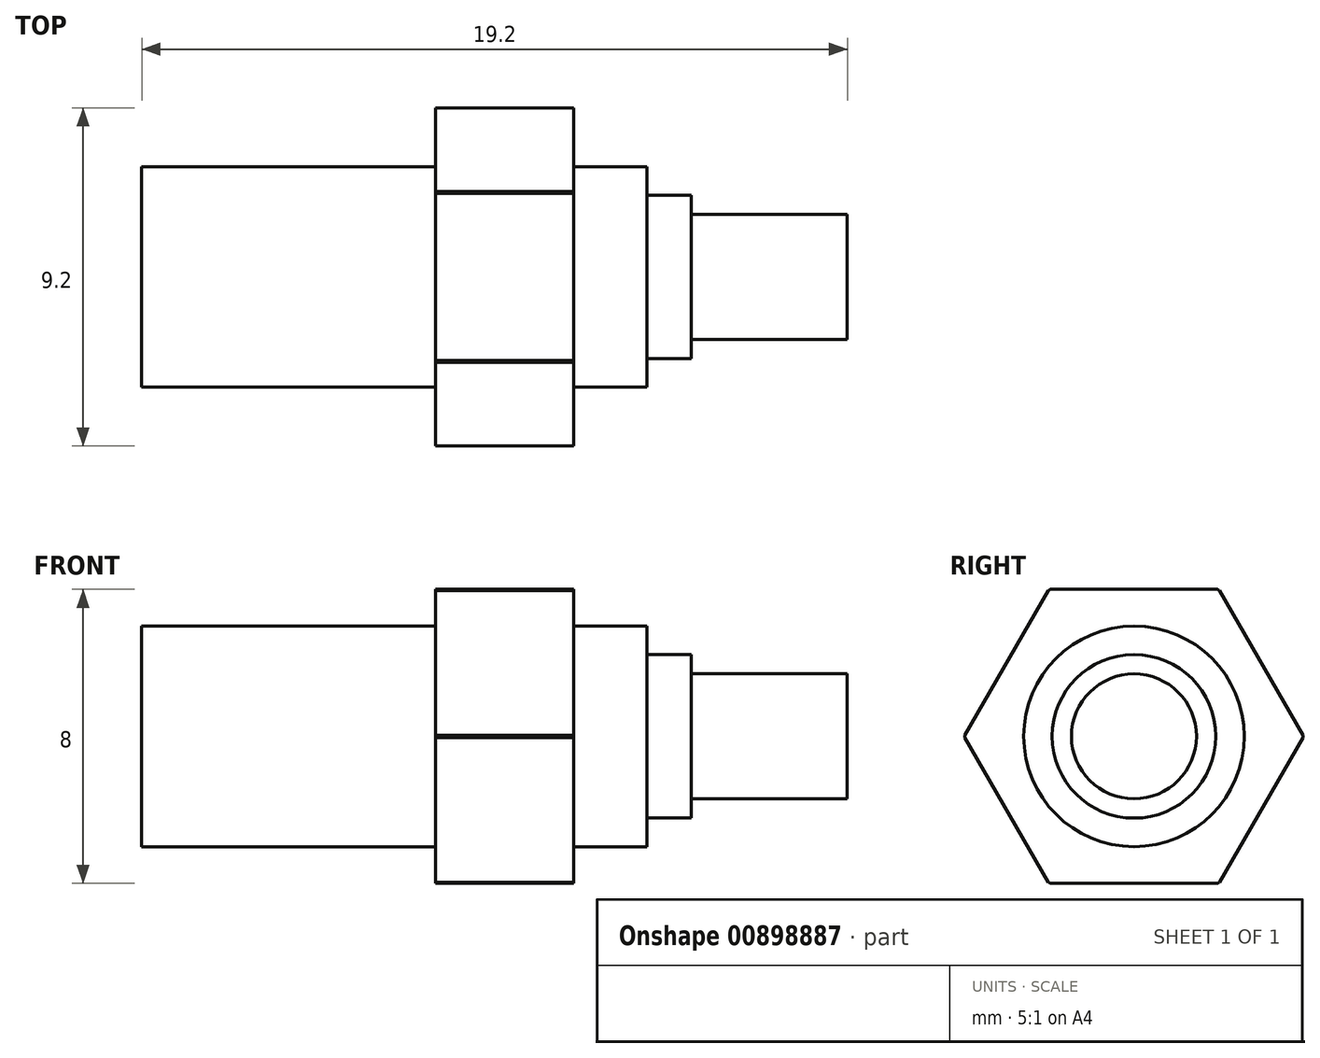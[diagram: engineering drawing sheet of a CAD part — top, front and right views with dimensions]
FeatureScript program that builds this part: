
annotation { "Feature Type Name" : "Feature", "Feature Type Description" : "" }
export const myFeature = defineFeature(function(context is Context, id is Id, definition is map)
    precondition{}
    {
        {
            var Q0;
            Q0=qCreatedBy(makeId("Top.planeOp"),FACE);
            var sketch = newSketch(context, id + "F0", { "sketchPlane" : qUnion([Q0])});
            skLineSegment(sketch, "E0", {"start": v(-9.92, 0) * mm, "end": v(9.28, 0) * mm});
            skLineSegment(sketch, "E1", {"start": v(9.28, 0) * mm, "end": v(9.28, 1.7) * mm});
            skLineSegment(sketch, "E2", {"start": v(9.28, 1.7) * mm, "end": v(5.03, 1.7) * mm});
            skLineSegment(sketch, "E3", {"start": v(5.03, 1.7) * mm, "end": v(5.03, 2.23) * mm});
            skLineSegment(sketch, "E4", {"start": v(5.03, 2.22) * mm, "end": v(3.83, 2.22) * mm});
            skLineSegment(sketch, "E5", {"start": v(3.83, 2.22) * mm, "end": v(3.83, 3) * mm});
            skLineSegment(sketch, "E6", {"start": v(3.83, 3) * mm, "end": v(1.83, 3) * mm});
            skLineSegment(sketch, "E7", {"start": v(1.83, 3) * mm, "end": v(1.83, 4.6) * mm});
            skLineSegment(sketch, "E8", {"start": v(1.83, 4.6) * mm, "end": v(-1.92, 4.6) * mm});
            skLineSegment(sketch, "E9", {"start": v(-1.92, 4.6) * mm, "end": v(-1.92, 3) * mm});
            skLineSegment(sketch, "E10", {"start": v(-1.92, 3) * mm, "end": v(-9.92, 3) * mm});
            skLineSegment(sketch, "E11", {"start": v(-9.92, 3) * mm, "end": v(-9.92, 0) * mm});
            skSolve(sketch);
        }
        {
            var Q0;
            Q0=qSketchRegion(id+"F0",true);
            var Q1;
            Q1=sQuery(id+"F0.wireOp",EDGE,"E0");
            revolve(context, id + "F1", {"surfaceOperationType" : NewSurfaceOperationType.NEW, "entities" : qUnion([Q0]), "axis" : qUnion([Q1]), "revolveType" : RevolveType.FULL});
        }
        {
            var Q0;
            Q0=makeQuery(id+"F1.opRevolve","SWEPT_FACE",FACE,{"disambiguationData":[OSD([sQuery(id+"F0.wireOp",EDGE,"E9")])]});
            var sketch = newSketch(context, id + "F2", { "sketchPlane" : qUnion([Q0])});
            skCircle(sketch, "E12.cCircle", {"center": v(0, 0) * mm, "radius": 4 * mm, "construction": true});
            skLineSegment(sketch, "E12.0", {"start": v(-2.3, 4) * mm, "end": v(2.3, 4) * mm});
            skLineSegment(sketch, "E12.1", {"start": v(2.3, 4) * mm, "end": v(4.62, 0) * mm});
            skLineSegment(sketch, "E12.2", {"start": v(4.62, 0) * mm, "end": v(2.3, -4) * mm});
            skLineSegment(sketch, "E12.3", {"start": v(2.3, -4) * mm, "end": v(-2.3, -4) * mm});
            skLineSegment(sketch, "E12.4", {"start": v(-2.3, -4) * mm, "end": v(-4.62, 0) * mm});
            skLineSegment(sketch, "E12.5", {"start": v(-4.62, 0) * mm, "end": v(-2.3, 4) * mm});
            skPoint(sketch, "E12.0.midPoint", {"position": v(0, 4) * mm});
            skSolve(sketch);
        }
        {
            var Q0;
            Q0=qSketchRegion(id+"F2",true);
            extrude(context, id + "F3", {"entities" : qUnion([Q0]), "operationType" : NewBodyOperationType.INTERSECT, "oppositeDirection" : true, "depth" : 25 * mm, "offsetDistance" : 25 * mm, "hasSecondDirection" : true, "secondDirectionOppositeDirection" : false, "secondDirectionDepth" : 13.9 * mm});
        }
    });
